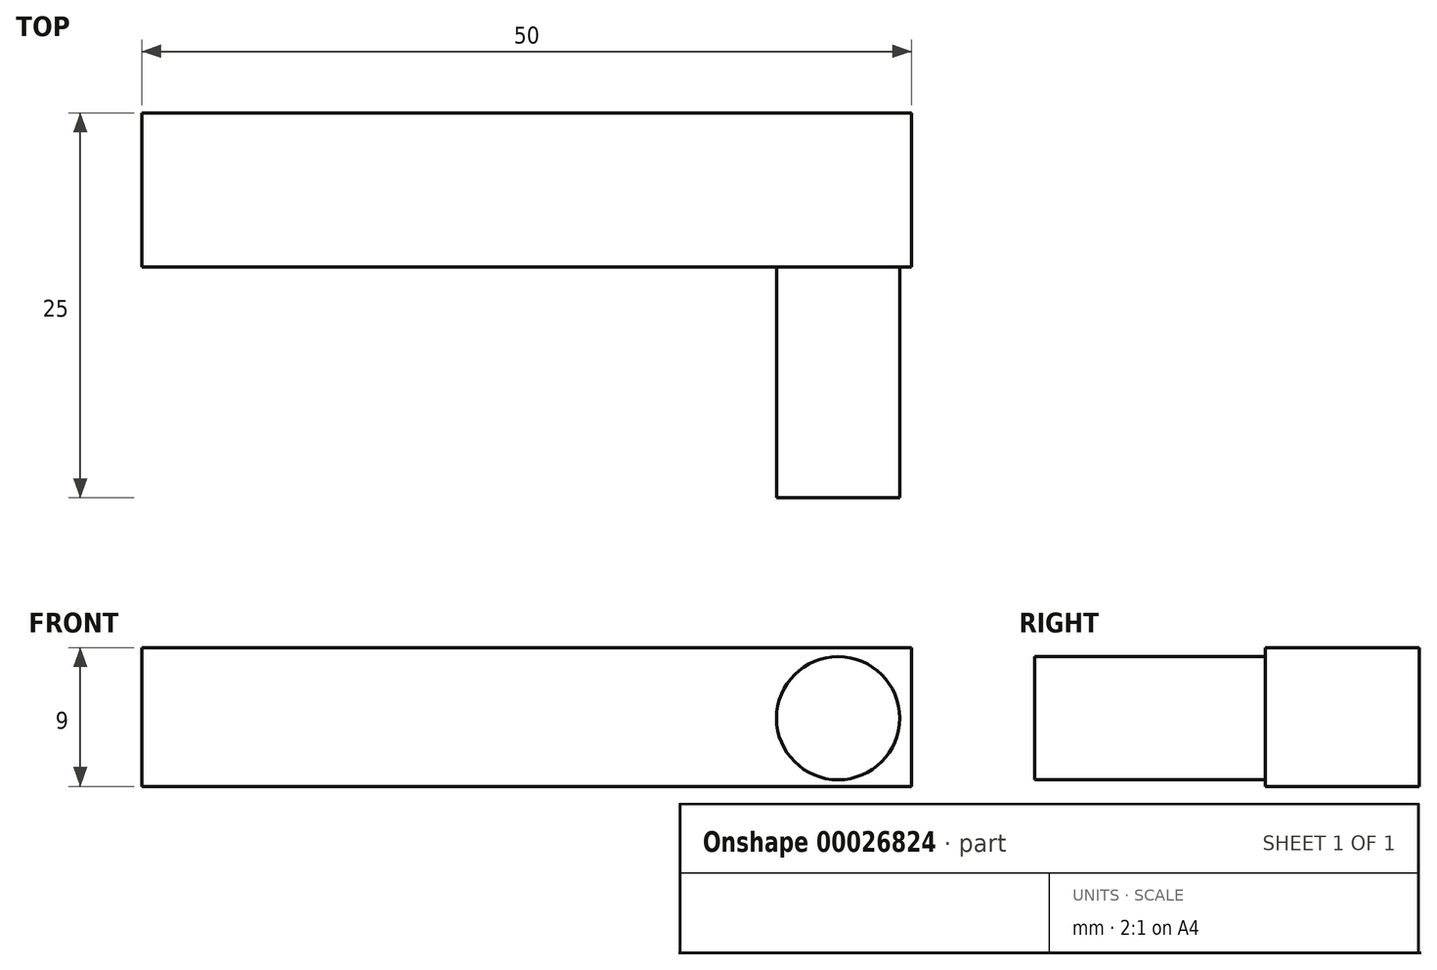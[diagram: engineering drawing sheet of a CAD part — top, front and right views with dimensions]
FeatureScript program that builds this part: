
annotation { "Feature Type Name" : "Feature", "Feature Type Description" : "" }
export const myFeature = defineFeature(function(context is Context, id is Id, definition is map)
    precondition{}
    {
        {
            var Q0;
            Q0=qCreatedBy(makeId("Front.planeOp"),FACE);
            var sketch = newSketch(context, id + "F0", { "sketchPlane" : qUnion([Q0])});
            skLineSegment(sketch, "E0.bottom", {"start": v(-68.9, 18.03) * mm, "end": v(-18.9, 18.03) * mm});
            skLineSegment(sketch, "E0.top", {"start": v(-68.9, 9.03) * mm, "end": v(-18.9, 9.03) * mm});
            skLineSegment(sketch, "E0.left", {"start": v(-68.9, 18.03) * mm, "end": v(-68.9, 9.03) * mm});
            skLineSegment(sketch, "E0.right", {"start": v(-18.9, 18.03) * mm, "end": v(-18.9, 9.03) * mm});
            skCircle(sketch, "E1", {"center": v(-23.67, 13.45) * mm, "radius": 4 * mm});
            skSolve(sketch);
        }
        {
            var Q0;
            Q0=makeQuery(id+"F0.imprint","IMPRINT",FACE,{"disambiguationData":[TD([[makeQuery(id+"F0.imprint","IMPRINT",EDGE,{"derivedFrom":sQuery(id+"F0.wireOp",EDGE,"E1")}),1.0]])]});
            extrude(context, id + "F1", {"entities" : qUnion([Q0]), "depth" : 25 * mm});
        }
        {
            var Q0;
            Q0=makeQuery(id+"F0.imprint","IMPRINT",FACE,{"disambiguationData":[TD([[makeQuery(id+"F0.imprint","IMPRINT",EDGE,{"derivedFrom":sQuery(id+"F0.wireOp",EDGE,"E0.bottom")}),-1.0]])]});
            extrude(context, id + "F2", {"entities" : qUnion([Q0]), "operationType" : NewBodyOperationType.ADD, "depth" : 10 * mm});
        }
    });
